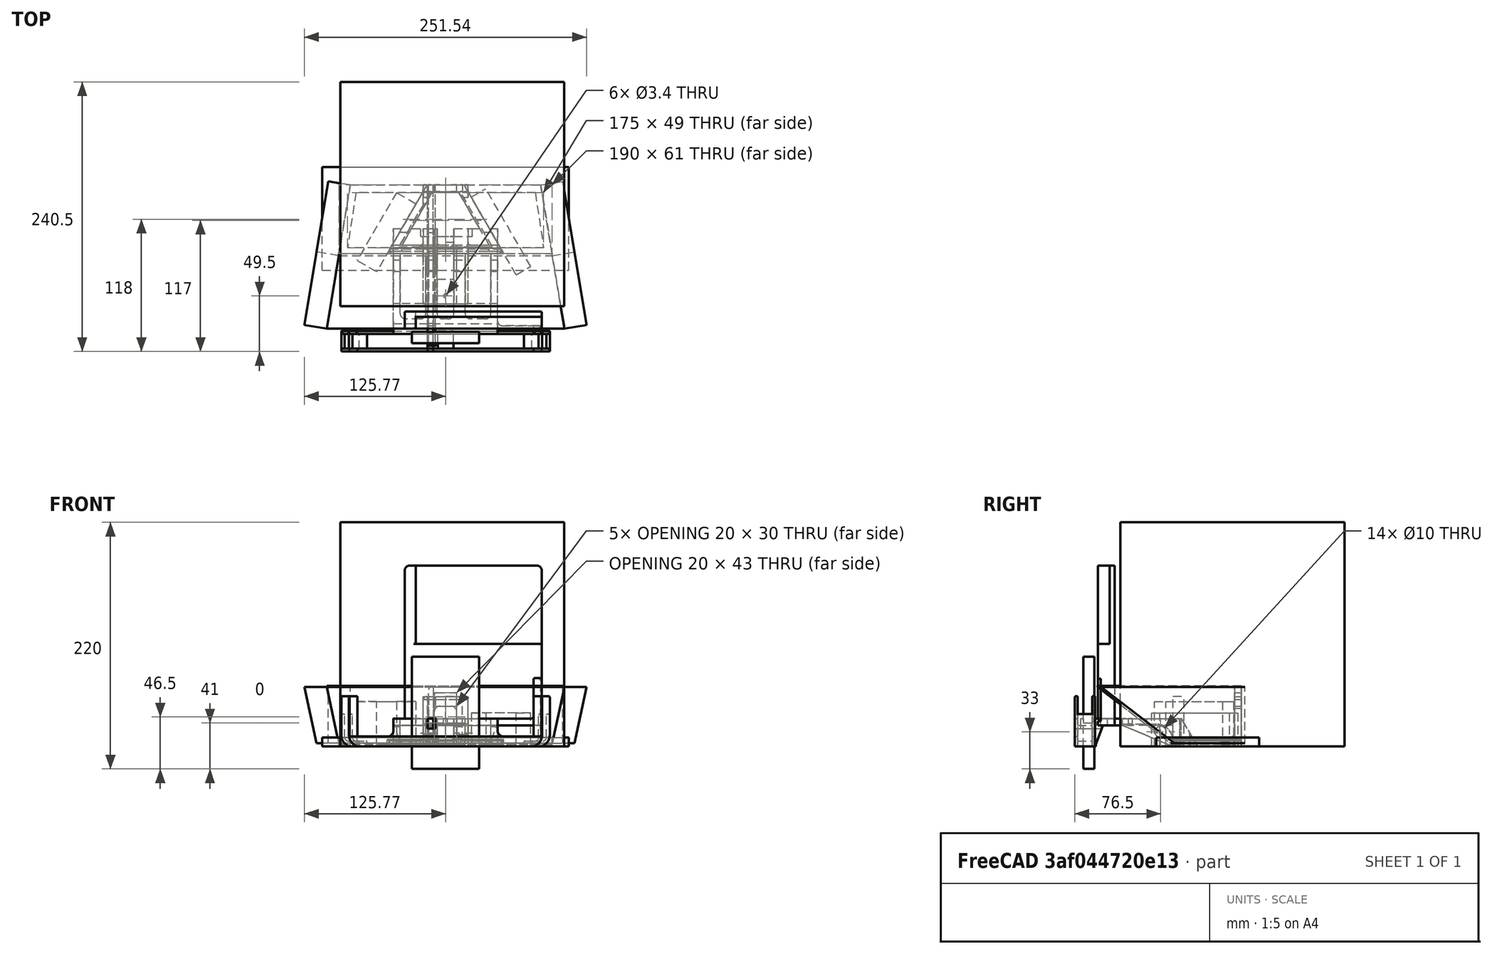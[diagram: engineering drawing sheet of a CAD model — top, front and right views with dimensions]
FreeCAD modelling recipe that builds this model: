
FCSTD DOCUMENT  (FreeCAD 0.20R29603 (Git))
Label: soporte_celular_auto_v3
License: All rights reserved
LicenseURL: http://en.wikipedia.org/wiki/All_rights_reserved
objects: Part::Box×88, Part::Cut×65, Part::Fillet×48, Part::MultiFuse×26, Part::Feature×24, Sketcher::SketchObject×14, Part::Extrusion×12, Part::Cylinder×5, Mesh::Feature×5, Part::Prism×4, PartDesign::Pad×3, PartDesign::Body×3, Part::Chamfer×2, PartDesign::ShapeBinder×2, PartDesign::SubShapeBinder×1
note: 300 computed .brp shape members not serialized (recipe doc carries the construction recipe); baked Part::Feature solids carry a one-line shape summary decoded from their .brp

FEATURE [Sketcher::SketchObject] Sketch001
  FullyConstrained = false
  sketch-geometry (4):
    g0: LineSegment StartX=-95 StartY=0 StartZ=0 EndX=95 EndY=-9e-16 EndZ=0
    g1: LineSegment StartX=-95 StartY=0 StartZ=0 EndX=-85 EndY=61 EndZ=0
    g2: LineSegment StartX=95 StartY=-9e-16 StartZ=0 EndX=85 EndY=61 EndZ=0
    g3: LineSegment StartX=-85 StartY=61 StartZ=0 EndX=85 EndY=61 EndZ=0
  constraints (10):
    c: PointOnObject(g0,g-1)
    c: Symmetric(g0,g0,g-2)
    c: DistanceX(g0,g0) = 190
    c: Coincident(g1,g0)
    c: Coincident(g2,g0)
    c: Coincident(g3,g1)
    c: Coincident(g3,g2)
    c: Symmetric(g1,g2,g-2)
    c: DistanceX(g3,g3) = 170
    c: DistanceY(g0,g2) = 61
FEATURE [Part::Extrusion] Extrude
  Base = -> Sketch001
  Dir = (0,0,1)
  DirMode = 2
  FaceMakerClass = Part::FaceMakerBullseye
  LengthFwd = 10
  LengthRev = 0
  Solid = true
  Symmetric = false
FEATURE [Part::Box] Box  label="Cube"
  AttacherType = Attacher::AttachEngine3D
  Height = 8
  Length = 220
  Placement = pos=(-110,-15,0) rot=(0,0,1;0rad)
  Width = 92
FEATURE [Part::Cut] Cut  label="molde_cortador"
  Base = -> Box
  Tool = -> Extrude
FEATURE [Part::Prism] Prism002
  AttacherType = Attacher::AttachEngine3D
  Circumradius = 60
  FirstAngle = 0
  Height = 6
  Placement = pos=(0,23,0) rot=(0,0,-1;0.523599rad)
  Polygon = 3
  SecondAngle = 0
FEATURE [Part::Prism] Prism003
  AttacherType = Attacher::AttachEngine3D
  Circumradius = 45
  FirstAngle = 0
  Height = 6
  Placement = pos=(0,23,0) rot=(0,0,-1;0.523599rad)
  Polygon = 3
  SecondAngle = 0
FEATURE [Part::Cut] Cut001
  Base = -> Prism002
  Placement = pos=(0,7,0) rot=(0,0,1;0rad)
  Tool = -> Prism003
FEATURE [Part::Box] Box001  label="Cube001"
  AttacherType = Attacher::AttachEngine3D
  Height = 6
  Length = 32
  Placement = pos=(-16,55,0) rot=(0,0,1;0rad)
  Width = 6
FEATURE [Part::MultiFuse] Fusion
  Shapes = -> [Cut001,Box001]
FEATURE [Sketcher::SketchObject] Sketch002
  FullyConstrained = false
  sketch-geometry (4):
    g0: LineSegment StartX=-95 StartY=0 StartZ=0 EndX=95 EndY=-9e-16 EndZ=0
    g1: LineSegment StartX=-95 StartY=0 StartZ=0 EndX=-85 EndY=61 EndZ=0
    g2: LineSegment StartX=95 StartY=-9e-16 StartZ=0 EndX=85 EndY=61 EndZ=0
    g3: LineSegment StartX=-85 StartY=61 StartZ=0 EndX=85 EndY=61 EndZ=0
  constraints (10):
    c: PointOnObject(g0,g-1)
    c: Symmetric(g0,g0,g-2)
    c: DistanceX(g0,g0) = 190
    c: Coincident(g1,g0)
    c: Coincident(g2,g0)
    c: Coincident(g3,g1)
    c: Coincident(g3,g2)
    c: Symmetric(g1,g2,g-2)
    c: DistanceX(g3,g3) = 170
    c: DistanceY(g0,g2) = 61
FEATURE [Part::Box] Box002  label="Cube002"
  AttacherType = Attacher::AttachEngine3D
  Height = 8
  Length = 220
  Placement = pos=(-110,-15,0) rot=(0,0,1;0rad)
  Width = 113
FEATURE [Part::Extrusion] Extrude001
  Base = -> Sketch002
  Dir = (0,0,1)
  DirMode = 2
  FaceMakerClass = Part::FaceMakerBullseye
  LengthFwd = 10
  LengthRev = 0
  Solid = true
  Symmetric = false
FEATURE [Part::Cut] Cut002  label="molde_cortador001"
  Base = -> Box002
  Tool = -> Extrude001
FEATURE [Part::Cut] Cut003  label="base_triangulo"
  Base = -> Fusion
  Tool = -> Cut002
FEATURE [Part::Box] Box003  label="Cube003"
  AttacherType = Attacher::AttachEngine3D
  Height = 3
  Length = 220
  Placement = pos=(-110,2,0) rot=(0,0,1;0rad)
  Width = 2.5
FEATURE [Part::Cut] Cut004  label="base_triangulo_con_canaleta"
  Base = -> Cut003
  Tool = -> Box003
FEATURE [Part::Feature] Fusion001
  shape: bbox 190 x 63 x 3 mm, 10 faces (baked)
FEATURE [Sketcher::SketchObject] Sketch003
  ExternalGeometry = -> [Fusion001]
  FullyConstrained = false
  sketch-geometry (4):
    g0: LineSegment StartX=-87.5 StartY=0 StartZ=0 EndX=87.5 EndY=0 EndZ=0
    g1: LineSegment StartX=-87.5 StartY=0 StartZ=0 EndX=-80 EndY=49 EndZ=0
    g2: LineSegment StartX=87.5 StartY=0 StartZ=0 EndX=80 EndY=49 EndZ=0
    g3: LineSegment StartX=-80 StartY=49 StartZ=0 EndX=80 EndY=49 EndZ=0
  constraints (10):
    c: PointOnObject(g0,g-1)
    c: Symmetric(g0,g0,g-2)
    c: DistanceX(g0,g0) = 175
    c: Coincident(g1,g0)
    c: Coincident(g2,g0)
    c: Coincident(g3,g1)
    c: Coincident(g3,g2)
    c: Symmetric(g1,g2,g-2)
    c: DistanceX(g3,g3) = 160
    c: DistanceY(g0,g2) = 49
FEATURE [Part::Extrusion] Extrude002
  Base = -> Sketch003
  Dir = (0,0,1)
  DirMode = 2
  FaceMakerClass = Part::FaceMakerBullseye
  LengthFwd = 10
  LengthRev = 0
  Placement = pos=(0,5,0) rot=(0,0,1;0rad)
  Solid = true
  Symmetric = false
FEATURE [Part::Cut] Cut004002  label="base"
  Base = -> Fusion001
  Tool = -> Extrude002
FEATURE [Sketcher::SketchObject] Sketch004
  ExternalGeometry = -> [Cut004002]
  FullyConstrained = false
  MapMode = 5
  Placement = pos=(-92.5137,15.1662,-3.7e-15) rot=(-0.51489,0.606172,0.606172;4.09257rad)
  Support = -> [Cut004002]
  sketch-geometry (4):
    g0: LineSegment StartX=-46.4456 StartY=3 StartZ=0 EndX=17.3423 EndY=3 EndZ=0
    g1: LineSegment StartX=-46.4456 StartY=3 StartZ=0 EndX=-46.4456 EndY=53 EndZ=0
    g2: LineSegment StartX=-46.4456 StartY=53 StartZ=0 EndX=83.5544 EndY=53 EndZ=0
    g3: LineSegment StartX=83.5544 StartY=53 StartZ=0 EndX=17.3423 EndY=3 EndZ=0
  constraints (10):
    c: Coincident(g0,g-4)
    c: Coincident(g0,g-3)
    c: Vertical(g1)
    c: Coincident(g0,g1)
    c: DistanceY(g1,g1) = 50
    c: Coincident(g2,g1)
    c: Horizontal(g2)
    c: DistanceX(g2,g2) = 130
    c: Coincident(g3,g2)
    c: Coincident(g3,g0)
FEATURE [Part::Feature] Fusion002
  shape: bbox 190 x 63 x 3 mm, 10 faces (baked)
FEATURE [Sketcher::SketchObject] Sketch005
  ExternalGeometry = -> [Fusion002]
  FullyConstrained = false
  sketch-geometry (4):
    g0: LineSegment StartX=-87.5 StartY=0 StartZ=0 EndX=87.5 EndY=0 EndZ=0
    g1: LineSegment StartX=-87.5 StartY=0 StartZ=0 EndX=-80 EndY=49 EndZ=0
    g2: LineSegment StartX=87.5 StartY=0 StartZ=0 EndX=80 EndY=49 EndZ=0
    g3: LineSegment StartX=-80 StartY=49 StartZ=0 EndX=80 EndY=49 EndZ=0
  constraints (10):
    c: PointOnObject(g0,g-1)
    c: Symmetric(g0,g0,g-2)
    c: DistanceX(g0,g0) = 175
    c: Coincident(g1,g0)
    c: Coincident(g2,g0)
    c: Coincident(g3,g1)
    c: Coincident(g3,g2)
    c: Symmetric(g1,g2,g-2)
    c: DistanceX(g3,g3) = 160
    c: DistanceY(g0,g2) = 49
FEATURE [Part::Extrusion] Extrude003
  Base = -> Sketch005
  Dir = (0,0,1)
  DirMode = 2
  FaceMakerClass = Part::FaceMakerBullseye
  LengthFwd = 10
  LengthRev = 0
  Placement = pos=(0,5,0) rot=(0,0,1;0rad)
  Solid = true
  Symmetric = false
FEATURE [Part::Cut] Cut004003  label="base001"
  Base = -> Fusion002
  Tool = -> Extrude003
FEATURE [Sketcher::SketchObject] Sketch006
  ExternalGeometry = -> [Cut004003]
  FullyConstrained = false
  MapMode = 5
  Placement = pos=(92.5137,15.1662,-2.34e-14) rot=(0.51489,0.606172,0.606172;2.19062rad)
  Support = -> [Cut004003]
  sketch-geometry (4):
    g0: LineSegment StartX=-17.3423 StartY=3 StartZ=0 EndX=46.4456 EndY=3 EndZ=0
    g1: LineSegment StartX=46.4456 StartY=3 StartZ=0 EndX=46.4456 EndY=53 EndZ=0
    g2: LineSegment StartX=46.4456 StartY=53 StartZ=0 EndX=-83.5544 EndY=53 EndZ=0
    g3: LineSegment StartX=-83.5544 StartY=53 StartZ=0 EndX=-17.3423 EndY=3 EndZ=0
  constraints (10):
    c: Coincident(g0,g-4)
    c: Coincident(g0,g-3)
    c: Coincident(g1,g0)
    c: Vertical(g1)
    c: DistanceY(g1,g1) = 50
    c: Coincident(g2,g1)
    c: Horizontal(g2)
    c: Coincident(g3,g2)
    c: DistanceX(g2,g2) = 130
    c: Coincident(g0,g3)
FEATURE [Part::Extrusion] Extrude004
  Base = -> Sketch006
  Dir = (0.986828,0.161775,-2e-16)
  DirMode = 2
  FaceMakerClass = Part::FaceMakerBullseye
  LengthFwd = 20
  LengthRev = 0
  Solid = true
  Symmetric = false
FEATURE [Part::Extrusion] Extrude006
  Base = -> Sketch004
  Dir = (-0.986828,0.161775,-1e-16)
  DirMode = 2
  FaceMakerClass = Part::FaceMakerBullseye
  LengthFwd = 20
  LengthRev = 0
  Solid = true
  Symmetric = false
FEATURE [Sketcher::SketchObject] Sketch
  ExternalGeometry = -> [Extrude006,Extrude004]
  FullyConstrained = false
  sketch-geometry (4):
    g0: LineSegment StartX=-85 StartY=61 StartZ=0 EndX=85 EndY=61 EndZ=0
    g1: LineSegment StartX=-106.031 StartY=-67.2876 StartZ=0 EndX=106.031 EndY=-67.2876 EndZ=0
    g2: LineSegment StartX=-85 StartY=61 StartZ=0 EndX=-106.031 EndY=-67.2876 EndZ=0
    g3: LineSegment StartX=85 StartY=61 StartZ=0 EndX=106.031 EndY=-67.2876 EndZ=0
  constraints (8):
    c: Coincident(g0,g-3)
    c: Coincident(g0,g-4)
    c: Coincident(g1,g-3)
    c: Coincident(g1,g-4)
    c: Coincident(g0,g2)
    c: Coincident(g0,g3)
    c: Coincident(g1,g2)
    c: Coincident(g1,g3)
FEATURE [Part::Extrusion] Extrude007  label="techo_posicion"
  Base = -> Sketch
  Dir = (0,0,1)
  DirMode = 2
  FaceMakerClass = Part::FaceMakerBullseye
  LengthFwd = 1
  LengthRev = 0
  Placement = pos=(0,0,53) rot=(0,0,1;0rad)
  Solid = true
  Symmetric = false
FEATURE [Part::Box] Box004  label="Cube004"
  AttacherType = Attacher::AttachEngine3D
  Height = 44.5
  Length = 40
  Placement = pos=(-20,55,0) rot=(0,0,1;0rad)
  Width = 6
FEATURE [Part::Box] Box005  label="Cube005"
  AttacherType = Attacher::AttachEngine3D
  Height = 30
  Length = 20
  Placement = pos=(-10,55,6) rot=(0,0,1;0rad)
  Width = 6
FEATURE [Part::Cut] Cut004004  label="parte_trasera"
  Base = -> Box004
  Tool = -> Box005
FEATURE [Part::Box] Box006  label="Cube006"
  AttacherType = Attacher::AttachEngine3D
  Height = 6
  Length = 40
  Placement = pos=(0,0,20) rot=(0,0,1;0rad)
  Width = 51
FEATURE [Part::Box] Box007  label="Cube007"
  AttacherType = Attacher::AttachEngine3D
  Height = 6
  Length = 15
  Placement = pos=(12.5,22,20) rot=(0,0,1;0rad)
  Width = 70
FEATURE [Part::Cut] Cut004005
  Base = -> Box006
  Placement = pos=(-20,0,-1) rot=(0,0,1;0rad)
  Tool = -> Box007
FEATURE [Part::Cylinder] Cylinder
  Angle = 360
  AttacherType = Attacher::AttachEngine3D
  FirstAngle = 0
  Height = 30
  Placement = pos=(0,7,0) rot=(0,0,1;0rad)
  Radius = 1.7
  SecondAngle = 0
FEATURE [Part::Cut] Cut004006
  Base = -> Cut004005
  Placement = pos=(0,-45,0) rot=(0,0,1;0rad)
  Tool = -> Cylinder
FEATURE [Part::Box] Box008  label="celular"
  AttacherType = Attacher::AttachEngine3D
  Height = 100
  Length = 60
  Placement = pos=(-30,-80,-20) rot=(0,0,1;0rad)
  Width = 10
FEATURE [Part::Box] Box009  label="Cube008"
  AttacherType = Attacher::AttachEngine3D
  Height = 22
  Length = 12.5
  Placement = pos=(7.5,0,3) rot=(0,0,1;0rad)
  Width = 7.5
FEATURE [Part::Box] Box010  label="Cube009"
  AttacherType = Attacher::AttachEngine3D
  Height = 22
  Length = 12.5
  Placement = pos=(-20,0,3) rot=(0,0,1;0rad)
  Width = 7.5
FEATURE [Part::Feature] Fusion004001  label="Fusion005"
  shape: bbox 99.53 x 106 x 53 mm, 44 faces (baked)
FEATURE [Part::Fillet] Fillet006
  Base = -> Fusion004001
  Edges = 2 edges r=15: [Edge75,Edge79]
FEATURE [Part::Fillet] Fillet007
  Base = -> Fillet006
  Edges = 2 edges r=2: [Edge65,Edge67]
FEATURE [Part::Fillet] Fillet008  label="soporte_final_v2.1_00"
  Base = -> Fillet007
  Edges = 2 edges r=2: [Edge3,Edge19]
FEATURE [Part::Feature] Fillet008001  label="soporte_final_v2.002"
  shape: bbox 99.53 x 106 x 53 mm, 50 faces (baked)
FEATURE [Part::Box] Box011  label="Cube010"
  AttacherType = Attacher::AttachEngine3D
  Height = 100
  Length = 70
  Placement = pos=(10,-51,0) rot=(0,0,1;0rad)
  Width = 120
FEATURE [Part::Cut] Cut004007
  Base = -> Fillet008001
  Tool = -> Box011
FEATURE [Part::Box] Box012  label="Cube011"
  AttacherType = Attacher::AttachEngine3D
  Height = 100
  Length = 70
  Placement = pos=(-11,13,0) rot=(0,0,1;0rad)
  Width = 120
FEATURE [Part::Cut] Cut004008
  Base = -> Cut004007
  Tool = -> Box012
FEATURE [Part::Box] Box013  label="Cube012"
  AttacherType = Attacher::AttachEngine3D
  Height = 10
  Length = 40
  Placement = pos=(-60,0,2) rot=(0,0,1;0rad)
  Width = 70
FEATURE [Part::Cut] Cut004009
  Base = -> Cut004008
  Tool = -> Box013
FEATURE [Part::Box] Box014  label="Cube013"
  AttacherType = Attacher::AttachEngine3D
  Height = 50
  Length = 19
  Placement = pos=(-30,-60,0) rot=(0,0,1;0rad)
  Width = 60
FEATURE [Part::Cut] Cut004010
  Base = -> Cut004009
  Tool = -> Box014
FEATURE [Part::Box] Box015  label="Cube014"
  AttacherType = Attacher::AttachEngine3D
  Height = 30
  Length = 10
  Placement = pos=(-21,0,2) rot=(0,0,1;0rad)
  Width = 10
FEATURE [Part::Cut] Cut004011
  Base = -> Cut004010
  Tool = -> Box015
FEATURE [Part::Fillet] Fillet008002  label="soporte_final_v2.1"
  Base = -> Fillet008
  Edges = 4 edges r=3: [Edge7,Edge53,Edge58,Edge60]
FEATURE [Part::Box] Box016  label="Cube015"
  AttacherType = Attacher::AttachEngine3D
  Height = 10
  Length = 40
  Placement = pos=(-54,-7,0) rot=(0,0,1;0rad)
  Width = 10
FEATURE [Part::Cut] Cut004012  label="test"
  Base = -> Cut004011
  Tool = -> Box016
FEATURE [Part::MultiFuse] Fusion004002
  Shapes = -> [Cut004006,Box009,Box010]
FEATURE [Part::Box] Box017  label="Cube016"
  AttacherType = Attacher::AttachEngine3D
  Height = 22
  Length = 12.5
  Placement = pos=(7.5,0,3) rot=(0,0,1;0rad)
  Width = 7.5
FEATURE [Part::Cylinder] Cylinder001
  Angle = 360
  AttacherType = Attacher::AttachEngine3D
  FirstAngle = 0
  Height = 30
  Placement = pos=(0,7,0) rot=(0,0,1;0rad)
  Radius = 1.7
  SecondAngle = 0
FEATURE [Part::Box] Box018  label="Cube017"
  AttacherType = Attacher::AttachEngine3D
  Height = 6
  Length = 40
  Placement = pos=(0,0,20) rot=(0,0,1;0rad)
  Width = 51
FEATURE [Part::Box] Box019  label="Cube018"
  AttacherType = Attacher::AttachEngine3D
  Height = 6
  Length = 15
  Placement = pos=(12.5,22,20) rot=(0,0,1;0rad)
  Width = 70
FEATURE [Part::Cut] Cut004013
  Base = -> Box018
  Placement = pos=(-20,0,-1) rot=(0,0,1;0rad)
  Tool = -> Box019
FEATURE [Part::Cut] Cut004014
  Base = -> Cut004013
  Placement = pos=(0,-45,0) rot=(0,0,1;0rad)
  Tool = -> Cylinder001
FEATURE [Part::Box] Box020  label="Cube019"
  AttacherType = Attacher::AttachEngine3D
  Height = 22
  Length = 12.5
  Placement = pos=(-20,0,3) rot=(0,0,1;0rad)
  Width = 7.5
FEATURE [Part::MultiFuse] Fusion004004
  Shapes = -> [Cut004014,Box017,Box020]
FEATURE [Sketcher::SketchObject] Sketch007
  ExternalGeometry = -> [Fusion004002,Cut004]
  FullyConstrained = true
  MapMode = 5
  Placement = pos=(-20,0,0) rot=(0.57735,-0.57735,-0.57735;2.0944rad)
  Support = -> [Fusion004002]
  sketch-geometry (3):
    g0: LineSegment StartX=0 StartY=0 StartZ=0 EndX=0 EndY=19 EndZ=0
    g1: LineSegment StartX=0 StartY=19 StartZ=0 EndX=45 EndY=19 EndZ=0
    g2: LineSegment StartX=45 StartY=19 StartZ=0 EndX=0 EndY=0 EndZ=0
  constraints (7):
    c: PointOnObject(g0,g-1)
    c: Vertical(g0)
    c: Coincident(g1,g0)
    c: Coincident(g0,g-3)
    c: Coincident(g1,g-3)
    c: Coincident(g2,g1)
    c: Coincident(g2,g0)
FEATURE [Part::Extrusion] Extrude008
  Base = -> Sketch007
  Dir = (-1,0,0)
  DirMode = 2
  FaceMakerClass = Part::FaceMakerBullseye
  LengthFwd = 0
  LengthRev = 39
  Placement = pos=(-26.5,0,0) rot=(0,0,1;0rad)
  Solid = true
  Symmetric = false
FEATURE [Part::Extrusion] Extrude009
  Base = -> Sketch007
  Dir = (-1,0,0)
  DirMode = 2
  FaceMakerClass = Part::FaceMakerBullseye
  LengthFwd = 39
  LengthRev = 0
  Placement = pos=(66.5,0,0) rot=(0,0,1;0rad)
  Solid = true
  Symmetric = false
FEATURE [Sketcher::SketchObject] Sketch008
  ExternalGeometry = -> [Fusion004002,Cut004]
  FullyConstrained = true
  MapMode = 5
  Placement = pos=(-20,0,0) rot=(0.57735,-0.57735,-0.57735;2.0944rad)
  Support = -> [Fusion004002]
  sketch-geometry (3):
    g0: LineSegment StartX=-7.5 StartY=0 StartZ=0 EndX=-7.5 EndY=25 EndZ=0
    g1: LineSegment StartX=-7.5 StartY=25 StartZ=0 EndX=-21.9338 EndY=0 EndZ=0
    g2: LineSegment StartX=-21.9338 StartY=0 StartZ=0 EndX=-7.5 EndY=0 EndZ=0
  constraints (8):
    c: Vertical(g0)
    c: Coincident(g0,g1)
    c: Coincident(g1,g2)
    c: Horizontal(g2)
    c: Coincident(g0,g2)
    c: Angle(g2,g1) = 1.0472
    c: DistanceY(g0,g-1) = 0
    c: Coincident(g0,g-3)
FEATURE [Part::Extrusion] Extrude010
  Base = -> Sketch008
  Dir = (-1,0,0)
  DirMode = 2
  FaceMakerClass = Part::FaceMakerBullseye
  LengthFwd = -39
  LengthRev = 0
  Placement = pos=(-26.5,0,0) rot=(0,0,1;0rad)
  Solid = true
  Symmetric = false
FEATURE [Part::Box] Box021  label="Cube020"
  AttacherType = Attacher::AttachEngine3D
  Height = 22
  Length = 12.5
  Placement = pos=(7.5,0,3) rot=(0,0,1;0rad)
  Width = 7.5
FEATURE [Sketcher::SketchObject] Sketch009
  FullyConstrained = false
  sketch-geometry (4):
    g0: LineSegment StartX=-95 StartY=0 StartZ=0 EndX=95 EndY=-9e-16 EndZ=0
    g1: LineSegment StartX=-95 StartY=0 StartZ=0 EndX=-85 EndY=61 EndZ=0
    g2: LineSegment StartX=95 StartY=-9e-16 StartZ=0 EndX=85 EndY=61 EndZ=0
    g3: LineSegment StartX=-85 StartY=61 StartZ=0 EndX=85 EndY=61 EndZ=0
  constraints (10):
    c: PointOnObject(g0,g-1)
    c: Symmetric(g0,g0,g-2)
    c: DistanceX(g0,g0) = 190
    c: Coincident(g1,g0)
    c: Coincident(g2,g0)
    c: Coincident(g3,g1)
    c: Coincident(g3,g2)
    c: Symmetric(g1,g2,g-2)
    c: DistanceX(g3,g3) = 170
    c: DistanceY(g0,g2) = 61
FEATURE [Part::Extrusion] Extrude011
  Base = -> Sketch009
  Dir = (0,0,1)
  DirMode = 2
  FaceMakerClass = Part::FaceMakerBullseye
  LengthFwd = 10
  LengthRev = 0
  Solid = true
  Symmetric = false
FEATURE [Part::Cylinder] Cylinder002
  Angle = 360
  AttacherType = Attacher::AttachEngine3D
  FirstAngle = 0
  Height = 30
  Placement = pos=(0,7,0) rot=(0,0,1;0rad)
  Radius = 1.7
  SecondAngle = 0
FEATURE [Part::Prism] Prism004
  AttacherType = Attacher::AttachEngine3D
  Circumradius = 45
  FirstAngle = 0
  Height = 6
  Placement = pos=(0,23,0) rot=(0,0,-1;0.523599rad)
  Polygon = 3
  SecondAngle = 0
FEATURE [Part::Box] Box022  label="Cube021"
  AttacherType = Attacher::AttachEngine3D
  Height = 6
  Length = 40
  Placement = pos=(0,0,20) rot=(0,0,1;0rad)
  Width = 51
FEATURE [Part::Box] Box023  label="Cube022"
  AttacherType = Attacher::AttachEngine3D
  Height = 3
  Length = 220
  Placement = pos=(-110,2,0) rot=(0,0,1;0rad)
  Width = 2.5
FEATURE [Part::Box] Box024  label="Cube023"
  AttacherType = Attacher::AttachEngine3D
  Height = 8
  Length = 220
  Placement = pos=(-110,-15,0) rot=(0,0,1;0rad)
  Width = 113
FEATURE [Part::Cut] Cut004020  label="molde_cortador002"
  Base = -> Box024
  Tool = -> Extrude011
FEATURE [Part::Prism] Prism005
  AttacherType = Attacher::AttachEngine3D
  Circumradius = 60
  FirstAngle = 0
  Height = 6
  Placement = pos=(0,23,0) rot=(0,0,-1;0.523599rad)
  Polygon = 3
  SecondAngle = 0
FEATURE [Part::Cut] Cut004019
  Base = -> Prism005
  Placement = pos=(0,7,0) rot=(0,0,1;0rad)
  Tool = -> Prism004
FEATURE [Part::Box] Box025  label="Cube024"
  AttacherType = Attacher::AttachEngine3D
  Height = 6
  Length = 15
  Placement = pos=(12.5,22,20) rot=(0,0,1;0rad)
  Width = 70
FEATURE [Part::Cut] Cut004017
  Base = -> Box022
  Placement = pos=(-20,0,-1) rot=(0,0,1;0rad)
  Tool = -> Box025
FEATURE [Part::Cut] Cut004018
  Base = -> Cut004017
  Placement = pos=(0,-45,0) rot=(0,0,1;0rad)
  Tool = -> Cylinder002
FEATURE [Part::Box] Box026  label="Cube025"
  AttacherType = Attacher::AttachEngine3D
  Height = 6
  Length = 32
  Placement = pos=(-16,55,0) rot=(0,0,1;0rad)
  Width = 6
FEATURE [Part::MultiFuse] Fusion004005
  Shapes = -> [Cut004019,Box026]
FEATURE [Part::Cut] Cut004015  label="base_triangulo001"
  Base = -> Fusion004005
  Tool = -> Cut004020
FEATURE [Part::Cut] Cut004016  label="base_triangulo_con_canaleta001"
  Base = -> Cut004015
  Tool = -> Box023
FEATURE [Part::Box] Box027  label="Cube026"
  AttacherType = Attacher::AttachEngine3D
  Height = 22
  Length = 12.5
  Placement = pos=(-20,0,3) rot=(0,0,1;0rad)
  Width = 7.5
FEATURE [Part::MultiFuse] Fusion004006
  Shapes = -> [Cut004018,Box021,Box027]
FEATURE [Sketcher::SketchObject] Sketch010
  ExternalGeometry = -> [Fusion004006,Cut004016]
  FullyConstrained = false
  MapMode = 5
  Placement = pos=(-20,0,0) rot=(0.57735,-0.57735,-0.57735;2.0944rad)
  Support = -> [Fusion004006]
  sketch-geometry (3):
    g0: LineSegment StartX=-7.5 StartY=0 StartZ=0 EndX=-7.5 EndY=25 EndZ=0
    g1: LineSegment StartX=-7.5 StartY=25 StartZ=0 EndX=-21.9338 EndY=0 EndZ=0
    g2: LineSegment StartX=-21.9338 StartY=0 StartZ=0 EndX=-7.5 EndY=0 EndZ=0
  constraints (8):
    c: Vertical(g0)
    c: Coincident(g0,g1)
    c: Coincident(g1,g2)
    c: Horizontal(g2)
    c: Coincident(g0,g2)
    c: Angle(g2,g1) = 1.0472
    c: DistanceY(g0,g-1) = 0
    c: Coincident(g0,g-3)
FEATURE [Part::Extrusion] Extrude012
  Base = -> Sketch010
  Dir = (-1,0,0)
  DirMode = 2
  FaceMakerClass = Part::FaceMakerBullseye
  LengthFwd = -39
  LengthRev = 0
  Placement = pos=(27.5,0,0) rot=(0,0,1;0rad)
  Solid = true
  Symmetric = false
FEATURE [Part::MultiFuse] Fusion004007
  Shapes = -> [Extrude010,Extrude012,Extrude009,Extrude008,Fusion004002]
FEATURE [Part::MultiFuse] Fusion004008  label="parte_frontal"
  Shapes = -> [Fusion004006,Fusion004007]
FEATURE [Part::MultiFuse] Fusion004009  label="pieza_sin_refinar"
  Shapes = -> [Cut004004,Cut004016,Fusion004008]
FEATURE [Part::Feature] Fusion004009001  label="pieza_sin_refinar001"
  shape: bbox 103.9 x 106 x 42 mm, 40 faces (baked)
FEATURE [Part::Fillet] Fillet
  Base = -> Fusion004009001
  Edges = 12 edges r=2: [Edge4,Edge8,Edge38,Edge44,Edge56,Edge57,Edge60,Edge62,Edge64,Edge66,Edge67,Edge68]
FEATURE [Part::Fillet] Fillet008003
  Base = -> Fillet
  Edges = 2 edges r=2: [Edge92,Edge98]
FEATURE [Part::Fillet] Fillet008004
  Base = -> Fillet008003
  Edges = 4 edges r=2: [Edge22,Edge28,Edge83,Edge88]
FEATURE [Part::Fillet] Fillet008005
  Base = -> Fillet008004
  Edges = 4 edges r=5: [Edge105,Edge107,Edge108,Edge111]
FEATURE [Part::Fillet] Fillet008006
  Base = -> Fillet008005
  Edges = 2 edges r=1: [Edge107,Edge131]
FEATURE [Part::Fillet] Fillet008007
  Base = -> Fillet008006
  Edges = 2 edges r=2: [Edge3,Edge23]
FEATURE [Part::Chamfer] Chamfer  label="soporte_v2.2"
  Base = -> Fillet008007
  Edges = 2 edges r=5: [Edge154,Edge156]
FEATURE [Part::Box] Box028  label="Cube027"
  AttacherType = Attacher::AttachEngine3D
  Height = 113
  Length = 109
  Placement = pos=(-10,-55,0) rot=(0,0,1;0rad)
  Width = 156
FEATURE [Part::Feature] Chamfer001  label="soporte_v2.2_for_test"
  shape: bbox 101 x 106 x 42 mm, 68 faces (baked)
FEATURE [Part::Cut] Cut004021  label="test_v2.2"
  Base = -> Chamfer001
  Tool = -> Box028
FEATURE [Part::Box] Box029  label="Cube028"
  AttacherType = Attacher::AttachEngine3D
  Height = 6
  Length = 78
  Placement = pos=(-39,0,0) rot=(0,0,1;0rad)
  Width = 15
FEATURE [Part::MultiFuse] Fusion004009002  label="pieza_sin_refinar_reforzada"
  Shapes = -> [Fusion004009,Box029]
FEATURE [Part::Box] Box030  label="Cube029"
  AttacherType = Attacher::AttachEngine3D
  Height = 45
  Length = 10
  Width = 10
FEATURE [Part::Box] Box031  label="Cube030"
  AttacherType = Attacher::AttachEngine3D
  Height = 16
  Length = 46
  Placement = pos=(-22,15,0) rot=(0,0,1;0rad)
  Width = 15
FEATURE [Part::Cut] Cut004022  label="pieza_sin_refinar_v2.3"
  Base = -> Fusion004009002
  Tool = -> Box031
FEATURE [Part::Feature] Cut004022001  label="pieza_sin_refinar_v2.004"
  shape: bbox 103.9 x 106 x 44.5 mm, 42 faces (baked)
FEATURE [Part::Fillet] Fillet008008
  Base = -> Cut004022001
  Edges = 2 edges r=5: [Edge111,Edge116]
FEATURE [Part::Fillet] Fillet008009
  Base = -> Fillet008008
  Edges = 4 edges r=5: [Edge69,Edge70,Edge71,Edge72]
FEATURE [Part::Fillet] Fillet008010
  Base = -> Fillet008009
  Edges = 2 edges r=5: [Edge41,Edge54]
FEATURE [Part::Fillet] Fillet008011
  Base = -> Fillet008010
  Edges = 4 edges r=3: [Edge73,Edge86,Edge90,Edge106]
FEATURE [Part::Fillet] Fillet008012
  Base = -> Fillet008011
  Edges = 2 edges r=3: [Edge130,Edge134]
FEATURE [Part::Fillet] Fillet008013
  Base = -> Fillet008012
  Edges = 4 edges r=3: [Edge54,Edge59,Edge71,Edge75]
FEATURE [Part::Fillet] Fillet008014  label="pieza_v2.3"
  Base = -> Fillet008013
  Edges = 4 edges r=3: [Edge10,Edge55,Edge72,Edge79]
FEATURE [Part::Box] Box032  label="Cube031"
  AttacherType = Attacher::AttachEngine3D
  Height = 22
  Length = 39
  Placement = pos=(7.5,0,3) rot=(0,0,1;0rad)
  Width = 7.5
FEATURE [Part::Box] Box033  label="Cube032"
  AttacherType = Attacher::AttachEngine3D
  Height = 22
  Length = 39
  Placement = pos=(-46.5,0,3) rot=(0,0,1;0rad)
  Width = 7.5
FEATURE [Part::MultiFuse] Fusion004009003
  Shapes = -> [Fusion004008,Box032,Box033]
FEATURE [Part::Box] Box034  label="Cube033"
  AttacherType = Attacher::AttachEngine3D
  Height = 6
  Length = 30
  Placement = pos=(-46.5,-45,19) rot=(0,0,1;0rad)
  Width = 50
FEATURE [Part::Box] Box035  label="Cube034"
  AttacherType = Attacher::AttachEngine3D
  Height = 6
  Length = 31
  Placement = pos=(15.5,-45,19) rot=(0,0,1;0rad)
  Width = 50
FEATURE [Part::MultiFuse] Fusion004009004
  Shapes = -> [Fillet008014,Fusion004009003,Box034,Box035]
FEATURE [Part::Box] Box036  label="Cube035"
  AttacherType = Attacher::AttachEngine3D
  Height = 3
  Length = 100
  Placement = pos=(-50,2,0) rot=(0,0,1;0rad)
  Width = 2.5
FEATURE [Part::Cut] Cut004022002
  Base = -> Fusion004009004
  Tool = -> Box036
FEATURE [PartDesign::ShapeBinder] CopyCut004022002
  TraceSupport = false
FEATURE [Sketcher::SketchObject] Sketch011
  FullyConstrained = true
  MapMode = 5
  Placement = pos=(38.9711,22.5,0) rot=(0.377964,0.654654,0.654654;2.41886rad)
  Support = -> [CopyCut004022002]
  sketch-geometry (4):
    g0: LineSegment StartX=-48 StartY=0 StartZ=0 EndX=-48 EndY=30 EndZ=0
    g1: LineSegment StartX=-48 StartY=30 StartZ=0 EndX=32 EndY=30 EndZ=0
    g2: LineSegment StartX=32 StartY=30 StartZ=0 EndX=32 EndY=0 EndZ=0
    g3: LineSegment StartX=32 StartY=0 StartZ=0 EndX=-48 EndY=0 EndZ=0
  constraints (12):
    c: PointOnObject(g0,g-1)
    c: Vertical(g0)
    c: Coincident(g0,g1)
    c: Horizontal(g1)
    c: Coincident(g1,g2)
    c: Vertical(g2)
    c: Coincident(g2,g3)
    c: Horizontal(g3)
    c: Coincident(g3,g0)
    c: DistanceX(g1,g1) = 80
    c: DistanceY(g0,g0) = 30
    c: DistanceX(g-1,g1) = 32
FEATURE [PartDesign::Pad] Pad
  Direction = (1,1,1)
  Length = 15
  Length2 = 100
  Profile = -> Sketch011
  Type = 0
FEATURE [PartDesign::Body] Body
  Group = -> [CopyCut004022002,Sketch011,Pad]
  Origin = -> Origin
  Tip = -> Pad
FEATURE [PartDesign::ShapeBinder] CopyCut004022002001
  TraceSupport = false
FEATURE [Sketcher::SketchObject] Sketch012
  FullyConstrained = true
  MapMode = 5
  Placement = pos=(-38.9711,22.5,0) rot=(-0.377964,0.654654,0.654654;3.86433rad)
  Support = -> [CopyCut004022002001]
  sketch-geometry (4):
    g0: LineSegment StartX=-25 StartY=0 StartZ=0 EndX=45 EndY=0 EndZ=0
    g1: LineSegment StartX=45 StartY=0 StartZ=0 EndX=45 EndY=40 EndZ=0
    g2: LineSegment StartX=45 StartY=40 StartZ=0 EndX=-25 EndY=40 EndZ=0
    g3: LineSegment StartX=-25 StartY=40 StartZ=0 EndX=-25 EndY=0 EndZ=0
  constraints (12):
    c: Coincident(g0,g1)
    c: Coincident(g1,g2)
    c: Coincident(g2,g3)
    c: Coincident(g3,g0)
    c: Horizontal(g0)
    c: Horizontal(g2)
    c: Vertical(g1)
    c: Vertical(g3)
    c: PointOnObject(g0,g-1)
    c: DistanceX(g2,g2) = 70
    c: DistanceY(g1,g1) = 40
    c: DistanceX(g0,g-1) = 25
FEATURE [PartDesign::Pad] Pad001
  Direction = (1,1,1)
  Length = 20
  Length2 = 100
  Profile = -> Sketch012
  Type = 0
FEATURE [PartDesign::Body] Body001
  Group = -> [CopyCut004022002001,Sketch012,Pad001]
  Origin = -> Origin001
  Tip = -> Pad001
FEATURE [Part::Feature] Cut004022002_solid  label="Cut004022002 (Solid)"
  shape: bbox 99.53 x 106 x 44.5 mm, 121 faces (baked)
FEATURE [Part::Feature] Body002
  shape: bbox 52.99 x 76.78 x 30 mm, 6 faces (baked)
FEATURE [Part::Feature] Body001001
  shape: bbox 52.32 x 70.62 x 40 mm, 6 faces (baked)
FEATURE [Part::Cut] Cut004022003
  Base = -> Cut004022002_solid
  Tool = -> Body002
FEATURE [Part::Cut] Cut004022004
  Base = -> Cut004022003
  Tool = -> Body001001
FEATURE [Part::Box] Box037  label="Cube036"
  AttacherType = Attacher::AttachEngine3D
  Height = 6
  Length = 93
  Placement = pos=(-46.5,-64.5,19) rot=(0,0,1;0rad)
  Width = 32
FEATURE [Part::MultiFuse] Fusion004009005
  Shapes = -> [Cut004022004,Box037]
FEATURE [Part::Box] Box038  label="Cube037"
  AttacherType = Attacher::AttachEngine3D
  Height = 30
  Length = 15
  Placement = pos=(-7.5,-58.5,0) rot=(0,0,1;0rad)
  Width = 50
FEATURE [Part::Box] Box039  label="Cube038"
  AttacherType = Attacher::AttachEngine3D
  Height = 30
  Length = 23
  Placement = pos=(17.5,-58.5,0) rot=(0,0,1;0rad)
  Width = 58.5
FEATURE [Part::Box] Box040  label="Cube039"
  AttacherType = Attacher::AttachEngine3D
  Height = 30
  Length = 23
  Placement = pos=(-40.5,-58.5,0) rot=(0,0,1;0rad)
  Width = 58.5
FEATURE [Part::Cut] Cut004022005
  Base = -> Fusion004009005
  Tool = -> Box038
FEATURE [Part::Cut] Cut004022006
  Base = -> Cut004022005
  Tool = -> Box040
FEATURE [Part::Cut] Cut004022007
  Base = -> Cut004022006
  Tool = -> Box039
FEATURE [Part::Fillet] Fillet008015
  Base = -> Cut004022007
  Edges = 4 edges r=5: [Edge49,Edge53,Edge65,Edge70]
FEATURE [Part::Fillet] Fillet008016
  Base = -> Fillet008015
  Edges = 4 edges r=1: [Edge28,Edge47,Edge61,Edge77]
FEATURE [Part::Fillet] Fillet008017
  Base = -> Fillet008016
  Edges = 1 edges r=1: [Edge269]
FEATURE [Part::Fillet] Fillet008018
  Base = -> Fillet008017
  Edges = 1 edges r=1: [Edge347]
FEATURE [Part::Fillet] Fillet008019
  Base = -> Fillet008018
  Edges = 2 edges r=5: [Edge236,Edge297]
FEATURE [Part::Fillet] Fillet008020
  Base = -> Fillet008019
  Edges = 2 edges r=3: [Edge392,Edge439]
FEATURE [Part::Cylinder] Cylinder003
  Angle = 360
  AttacherType = Attacher::AttachEngine3D
  FirstAngle = 0
  Height = 100
  Placement = pos=(-50,-11,13) rot=(0,1,0;1.5708rad)
  Radius = 5
  SecondAngle = 0
FEATURE [Part::Cut] Cut004022008  label="frontal_solo_soporte"
  Base = -> Fillet008020
  Tool = -> Cylinder003
FEATURE [Part::Box] Box041  label="base_sofporte_celular"
  AttacherType = Attacher::AttachEngine3D
  Height = 40
  Length = 166.2
  Width = 13
FEATURE [Part::Box] Box042  label="base_sofporte_celular001"
  AttacherType = Attacher::AttachEngine3D
  Height = 45
  Length = 172.2
  Placement = pos=(-3,-2.5,-5) rot=(0,0,1;0rad)
  Width = 18
FEATURE [Part::Cut] Cut004022009
  Base = -> Box042
  Placement = pos=(-83.1,-80,20) rot=(0,0,1;0rad)
  Tool = -> Box041
FEATURE [Part::Box] Box043  label="base_sofporte_celular002"
  AttacherType = Attacher::AttachEngine3D
  Height = 40
  Length = 157.2
  Placement = pos=(-78.6,-87.5,24) rot=(0,0,1;0rad)
  Width = 25
FEATURE [Part::Cut] Cut004022010
  Base = -> Cut004022009
  Tool = -> Box043
FEATURE [Part::Box] Box044  label="Cube040"
  AttacherType = Attacher::AttachEngine3D
  Height = 100
  Length = 100
  Placement = pos=(-9,-91,0) rot=(0,0,1;0rad)
  Width = 200
FEATURE [Part::Box] Box045  label="Cube041"
  AttacherType = Attacher::AttachEngine3D
  Height = 100
  Length = 100
  Placement = pos=(-115,-91,0) rot=(0,0,1;0rad)
  Width = 200
FEATURE [Part::Box] Box046  label="Cube042"
  AttacherType = Attacher::AttachEngine3D
  Height = 3
  Length = 6
  Placement = pos=(-15,0,0) rot=(0,0,1;0rad)
  Width = 57
FEATURE [Part::Box] Box047  label="Cube043"
  AttacherType = Attacher::AttachEngine3D
  Height = 29
  Length = 10
  Placement = pos=(-17,0,3) rot=(0,0,1;0rad)
  Width = 55
FEATURE [Part::Box] Box048  label="Cube044"
  AttacherType = Attacher::AttachEngine3D
  Height = 200
  Length = 200
  Placement = pos=(-100,-66,0) rot=(0,0,1;0rad)
  Width = 200
FEATURE [Part::Box] Box049  label="Cube045"
  AttacherType = Attacher::AttachEngine3D
  Height = 200
  Length = 200
  Placement = pos=(-100,-281,0) rot=(0,0,1;0rad)
  Width = 200
FEATURE [Part::Box] Box052  label="Cube048"
  AttacherType = Attacher::AttachEngine3D
  Height = 20
  Length = 140
  Placement = pos=(-70,-80,9) rot=(0,0,1;0rad)
  Width = 13
FEATURE [Part::Cut] Cut004022017  label="frontal_solo_celular1"
  Base = -> Cut004022010
  Placement = pos=(0,-5,-25) rot=(0,0,1;0rad)
  Tool = -> Box052
FEATURE [Part::Feature] Fillet008027011001  label="soporte_v3_003"
  shape: bbox 173.4 x 143.5 x 61 mm, 224 faces (baked)
FEATURE [Part::Cut] Cut004022018
  Base = -> Fillet008027011001
  Tool = -> Box045
FEATURE [Part::Cut] Cut004022019
  Base = -> Cut004022018
  Tool = -> Box044
FEATURE [Part::Box] Box053  label="Cube049"
  AttacherType = Attacher::AttachEngine3D
  Height = 5
  Length = 6
  Placement = pos=(-15,-82,16) rot=(0,0,1;0rad)
  Width = 17
FEATURE [Part::MultiFuse] Fusion004009009
  Shapes = -> [Cut004022019,Box046]
FEATURE [Part::MultiFuse] Fusion004009010
  Shapes = -> [Fusion004009009,Box053]
FEATURE [Part::Cut] Cut004022020
  Base = -> Fusion004009010
  Tool = -> Box047
FEATURE [Part::Chamfer] Chamfer002  label="test_v3_1"
  Base = -> Cut004022020
  Edges = 1 edges r=2: [Edge78]
FEATURE [Part::Feature] Fillet008027011008001  label="soporte_v3_004"
  shape: bbox 173.7 x 143.7 x 61.22 mm, 236 faces, 0 solids (baked)
FEATURE [Part::Cut] Cut004022021
  Base = -> Fillet008027011008001
  Tool = -> Box048
FEATURE [Part::Cut] Cut004022022  label="test_v3_2"
  Base = -> Cut004022021
  Tool = -> Box049
FEATURE [Mesh::Feature] Mesh002  label="test_v3_2 (Meshed)"
FEATURE [Part::Feature] Fillet008027011008_solid  label="soporte_v3_2 (Solid)"
  shape: bbox 173.7 x 143.7 x 61.22 mm, 236 faces (baked)
FEATURE [Part::Box] Box054  label="Cube050"
  AttacherType = Attacher::AttachEngine3D
  Height = 200
  Length = 200
  Placement = pos=(-94,-47,0) rot=(0,0,1;0rad)
  Width = 200
FEATURE [Part::Feature] Fillet008027011008_solid001  label="soporte_v3_2 (Solid)001"
  shape: bbox 173.7 x 143.7 x 61.22 mm, 236 faces (baked)
FEATURE [Part::Box] Box055  label="Cube051"
  AttacherType = Attacher::AttachEngine3D
  Height = 200
  Length = 200
  Placement = pos=(-94,-247,0) rot=(0,0,1;0rad)
  Width = 200
FEATURE [Part::Cut] Cut004022023
  Base = -> Fillet008027011008_solid
  Refine = true
  Tool = -> Box055
FEATURE [Part::Box] Box056  label="Cube052"
  AttacherType = Attacher::AttachEngine3D
  Height = 6
  Length = 93
  Placement = pos=(-46.5,-72,19) rot=(0,0,1;0rad)
  Width = 8
FEATURE [Part::Box] Box057  label="Cube053"
  AttacherType = Attacher::AttachEngine3D
  Height = 200
  Length = 200
  Placement = pos=(-216,-97,0) rot=(0,0,1;0rad)
  Width = 200
FEATURE [Part::Box] Box058  label="Cube054"
  AttacherType = Attacher::AttachEngine3D
  Height = 200
  Length = 200
  Placement = pos=(-11,-97,0) rot=(0,0,1;0rad)
  Width = 200
FEATURE [Part::Box] Box059  label="Cube055"
  AttacherType = Attacher::AttachEngine3D
  Height = 20
  Length = 10
  Placement = pos=(-18,40,6) rot=(0,0,1;0rad)
  Width = 15
FEATURE [Part::Feature] Body001002
  shape: bbox 52.99 x 76.78 x 30 mm, 6 faces (baked)
FEATURE [Part::Feature] Cut004022002_solid001  label="Cut004022002 (Solid)001"
  shape: bbox 99.53 x 106 x 44.5 mm, 121 faces (baked)
FEATURE [Part::Feature] Body001003
  shape: bbox 52.32 x 70.62 x 40 mm, 6 faces (baked)
FEATURE [Part::Cut] Cut004022026
  Base = -> Cut004022002_solid001
  Tool = -> Body001002
FEATURE [Part::Cut] Cut004022027
  Base = -> Cut004022026
  Tool = -> Body001003
FEATURE [Part::Box] Box060  label="Cube056"
  AttacherType = Attacher::AttachEngine3D
  Height = 30
  Length = 23
  Placement = pos=(-40.5,-58.5,0) rot=(0,0,1;0rad)
  Width = 58.5
FEATURE [Part::Box] Box061  label="base_sofporte_celular003"
  AttacherType = Attacher::AttachEngine3D
  Height = 40
  Length = 157.2
  Placement = pos=(-78.6,-87.5,24) rot=(0,0,1;0rad)
  Width = 25
FEATURE [Part::Box] Box062  label="Cube057"
  AttacherType = Attacher::AttachEngine3D
  Height = 30
  Length = 15
  Placement = pos=(-7.5,-58.5,0) rot=(0,0,1;0rad)
  Width = 50
FEATURE [Part::Cylinder] Cylinder004
  Angle = 360
  AttacherType = Attacher::AttachEngine3D
  FirstAngle = 0
  Height = 100
  Placement = pos=(-50,-11,13) rot=(0,1,0;1.5708rad)
  Radius = 5
  SecondAngle = 0
FEATURE [Part::Box] Box063  label="Cube058"
  AttacherType = Attacher::AttachEngine3D
  Height = 6
  Length = 93
  Placement = pos=(-46.5,-64.5,19) rot=(0,0,1;0rad)
  Width = 32
FEATURE [Part::MultiFuse] Fusion004009013
  Shapes = -> [Cut004022027,Box063]
FEATURE [Part::Cut] Cut004022025
  Base = -> Fusion004009013
  Tool = -> Box062
FEATURE [Part::Cut] Cut004022028
  Base = -> Cut004022025
  Tool = -> Box060
FEATURE [Part::Box] Box064  label="base_sofporte_celular004"
  AttacherType = Attacher::AttachEngine3D
  Height = 40
  Length = 166.2
  Width = 13
FEATURE [Part::Box] Box065  label="Cube059"
  AttacherType = Attacher::AttachEngine3D
  Height = 30
  Length = 23
  Placement = pos=(17.5,-58.5,0) rot=(0,0,1;0rad)
  Width = 58.5
FEATURE [Part::Cut] Cut004022024
  Base = -> Cut004022028
  Tool = -> Box065
FEATURE [Part::Fillet] Fillet008027011008008
  Base = -> Cut004022024
  Edges = 4 edges r=5: [Edge49,Edge53,Edge65,Edge70]
FEATURE [Part::Fillet] Fillet008027011008009
  Base = -> Fillet008027011008008
  Edges = 4 edges r=1: [Edge28,Edge47,Edge61,Edge77]
FEATURE [Part::Fillet] Fillet008027011008010
  Base = -> Fillet008027011008009
  Edges = 1 edges r=1: [Edge269]
FEATURE [Part::Fillet] Fillet008027011008011
  Base = -> Fillet008027011008010
  Edges = 1 edges r=1: [Edge347]
FEATURE [Part::Fillet] Fillet008027011008012
  Base = -> Fillet008027011008011
  Edges = 2 edges r=5: [Edge236,Edge297]
FEATURE [Part::Fillet] Fillet008027011008007
  Base = -> Fillet008027011008012
  Edges = 2 edges r=3: [Edge392,Edge439]
FEATURE [Part::Box] Box066  label="base_sofporte_celular005"
  AttacherType = Attacher::AttachEngine3D
  Height = 45
  Length = 172.2
  Placement = pos=(-3,-2.5,-5) rot=(0,0,1;0rad)
  Width = 18
FEATURE [Part::Cut] Cut004022030  label="frontal_solo_soporte001"
  Base = -> Fillet008027011008007
  Tool = -> Cylinder004
FEATURE [Part::Cut] Cut004022032
  Base = -> Box066
  Placement = pos=(-83.1,-80,20) rot=(0,0,1;0rad)
  Tool = -> Box064
FEATURE [Part::Cut] Cut004022031
  Base = -> Cut004022032
  Tool = -> Box061
FEATURE [Part::Box] Box067  label="Cube060"
  AttacherType = Attacher::AttachEngine3D
  Height = 6
  Length = 93
  Placement = pos=(-46.5,-70,19) rot=(0,0,1;0rad)
  Width = 6
FEATURE [Part::Box] Box068  label="Cube061"
  AttacherType = Attacher::AttachEngine3D
  Height = 20
  Length = 140
  Placement = pos=(-70,-80,9) rot=(0,0,1;0rad)
  Width = 13
FEATURE [Part::Cut] Cut004022029
  Base = -> Cut004022031
  Tool = -> Box068
FEATURE [Part::Fillet] Fillet008027011008018
  Base = -> Cut004022029
  Edges = 4 edges r=2: [Edge56,Edge58,Edge60,Edge62]
  Placement = pos=(0,-5,1) rot=(0,0,1;0rad)
FEATURE [Part::MultiFuse] Fusion004009012
  Refine = true
  Shapes = -> [Cut004022030,Fillet008027011008018,Box067]
FEATURE [Part::Box] Box069  label="Cube062"
  AttacherType = Attacher::AttachEngine3D
  Height = 3
  Length = 12
  Placement = pos=(-19,-86,16) rot=(0,0,1;0rad)
  Width = 15
FEATURE [Part::MultiFuse] Fusion004009014
  Refine = true
  Shapes = -> [Fusion004009012,Box069]
FEATURE [Part::Box] Box070  label="Cube063"
  AttacherType = Attacher::AttachEngine3D
  Height = 6
  Length = 12
  Placement = pos=(-19,17,0) rot=(0,0,1;0rad)
  Width = 40
FEATURE [Part::MultiFuse] Fusion004009015
  Refine = true
  Shapes = -> [Fusion004009014,Box070]
FEATURE [Part::Cut] Cut004022033
  Base = -> Fusion004009015
  Refine = true
  Tool = -> Box057
FEATURE [Part::Cut] Cut004022034
  Base = -> Cut004022033
  Refine = true
  Tool = -> Box058
FEATURE [Part::Cut] Cut004022035  label="test_v33_largo"
  Base = -> Cut004022034
  Refine = true
  Tool = -> Box059
FEATURE [Mesh::Feature] Mesh  label="test_v33_largo (Meshed)"
FEATURE [Part::Box] Box071  label="Cube064"
  AttacherType = Attacher::AttachEngine3D
  Height = 31
  Length = 93
  Placement = pos=(-46.5,-72,-10) rot=(0,0,1;0rad)
  Width = 2.5
FEATURE [Part::MultiFuse] Fusion004009016  label="union_frontal1"
  Shapes = -> [Box071,Box056]
FEATURE [Part::Box] Box072  label="Cube065"
  AttacherType = Attacher::AttachEngine3D
  Height = 31
  Length = 176
  Placement = pos=(-88,-85,19) rot=(0,0,1;0rad)
  Width = 13
FEATURE [Part::Cut] Cut004022036  label="frontal_solo_celular"
  Base = -> Cut004022017
  Tool = -> Box072
FEATURE [Sketcher::SketchObject] Sketch014
  FullyConstrained = true
  MapMode = 5
  Placement = pos=(0,0,0) rot=(0.57735,0.57735,0.57735;2.0944rad)
  Support = -> [YZ_Plane003]
  sketch-geometry (3):
    g0: LineSegment StartX=-69.5 StartY=-10 StartZ=0 EndX=-69.5 EndY=19 EndZ=0
    g1: LineSegment StartX=-69.5 StartY=19 StartZ=0 EndX=-58.9449 EndY=19 EndZ=0
    g2: LineSegment StartX=-58.9449 StartY=19 StartZ=0 EndX=-69.5 EndY=-10 EndZ=0
  constraints (9):
    c: Vertical(g0)
    c: Coincident(g0,g1)
    c: Horizontal(g1)
    c: Coincident(g1,g2)
    c: Coincident(g2,g0)
    c: Angle(g2,g0) = 0.349066
    c: DistanceY(g0,g-1) = 10
    c: DistanceY(g-1,g1) = 19
    c: DistanceX(g0,g-1) = 69.5
FEATURE [PartDesign::SubShapeBinder] Binder
  BindCopyOnChange = 0
  BindMode = 0
  ClaimChildren = false
  Context = -> Body001004 [Binder.]
  Fuse = false
  MakeFace = true
  OffsetFill = false
  OffsetIntersection = false
  OffsetJoinType = 0
  OffsetOpenResult = false
  PartialLoad = false
  Refine = true
  Relative = true
  Support = -> [Sketch014]
  _Version = 2
FEATURE [PartDesign::Pad] Pad002
  Direction = (1,1,1)
  Length = 93
  Length2 = 100
  Midplane = true
  Profile = -> Binder
  Type = 0
FEATURE [PartDesign::Body] Body001004
  Group = -> [Binder,Pad002]
  Origin = -> Origin002
  Tip = -> Pad002
FEATURE [Part::MultiFuse] Fusion004009017  label="union_frontal002"
  Placement = pos=(0,0,10) rot=(0,0,1;0rad)
  Shapes = -> [Fusion004009016,Body001004]
FEATURE [Part::Fillet] Fillet008027011008019
  Base = -> Cut004022036
  Edges = 2 edges r=10: [Edge7,Edge29]
FEATURE [Part::Fillet] Fillet008027011008020
  Base = -> Fillet008027011008019
  Edges = 2 edges r=3: [Edge78,Edge104]
FEATURE [Part::Fillet] Fillet008027011008021
  Base = -> Fillet008027011008020
  Edges = 15 edges r=1: [Edge32,Edge53,Edge64,Edge72,Edge80,Edge89,Edge93,Edge95,Edge97,Edge99,Edge100,Edge101,Edge104,Edge106,Edge107]
FEATURE [Part::Fillet] Fillet008027011008022
  Base = -> Fillet008027011008021
  Edges = 3 edges r=1: [Edge79,Edge86,Edge90]
FEATURE [Part::Fillet] Fillet008027011008023  label="soporte_celular_frontal1"
  Base = -> Fillet008027011008022
  Edges = 10 edges r=1: [Edge17,Edge23,Edge27,Edge54,Edge58,Edge60,Edge89,Edge92,Edge95,Edge103]
  Placement = pos=(0,0,10) rot=(0,0,1;0rad)
FEATURE [Part::Box] Box073  label="Cube066"
  AttacherType = Attacher::AttachEngine3D
  Height = 12
  Length = 93
  Placement = pos=(-46.5,-72,25) rot=(0,0,1;0rad)
  Width = 14
FEATURE [Part::Cut] Cut004022037  label="union_frontal"
  Base = -> Fusion004009017
  Tool = -> Box073
FEATURE [Part::Fillet] Fillet008027011008024  label="union_frontal_redondeado"
  Base = -> Cut004022037
  Edges = 1 edges r=5: [Edge10]
FEATURE [Part::Fillet] Fillet008027011008025  label="frontal_celular_redondeado"
  Base = -> Fillet008027011008023
  Edges = 2 edges r=1: [Edge69,Edge121]
FEATURE [Part::MultiFuse] Fusion004009018
  Shapes = -> [Fillet008027011008025,Fillet008027011008024,Cut004022008]
FEATURE [Part::Fillet] Fillet008027011008026  label="soporte_v4"
  Base = -> Fusion004009018
  Edges = 2 edges r=5: [Edge156,Edge212]
FEATURE [Mesh::Feature] Mesh003  label="soporte_v4 (Meshed)"
FEATURE [Part::Feature] Fillet008027011008026001  label="soporte_v4_tablet1"
  shape: bbox 172.2 x 148.5 x 45 mm, 254 faces (baked)
FEATURE [Part::Feature] Fillet008027011008026002  label="soporte_v4_tablet2"
  shape: bbox 172.2 x 148.5 x 45 mm, 254 faces (baked)
FEATURE [Part::Feature] Fillet008027011008026003  label="soporte_v4_tablet3"
  shape: bbox 172.2 x 148.5 x 45 mm, 254 faces (baked)
FEATURE [Part::Box] Box074  label="Cube067"
  AttacherType = Attacher::AttachEngine3D
  Height = 80
  Length = 200
  Placement = pos=(-54,-111,-5) rot=(0,0,1;0rad)
  Width = 200
FEATURE [Part::Box] Box075  label="Cube068"
  AttacherType = Attacher::AttachEngine3D
  Height = 80
  Length = 200
  Placement = pos=(-254,-111,-5) rot=(0,0,1;0rad)
  Width = 200
FEATURE [Part::Box] Box076  label="Cube069"
  AttacherType = Attacher::AttachEngine3D
  Height = 80
  Length = 200
  Placement = pos=(-146,-111,-5) rot=(0,0,1;0rad)
  Width = 200
FEATURE [Part::Box] Box078  label="Cube071"
  AttacherType = Attacher::AttachEngine3D
  Height = 80
  Length = 200
  Placement = pos=(54,-111,-5) rot=(0,0,1;0rad)
  Width = 200
FEATURE [Part::Cut] Cut004022038  label="izquierda"
  Base = -> Fillet008027011008026001
  Placement = pos=(-6.9,0,0) rot=(0,0,1;0rad)
  Tool = -> Box074
FEATURE [Part::Cut] Cut004022039
  Base = -> Fillet008027011008026002
  Tool = -> Box078
FEATURE [Part::Cut] Cut004022040  label="centro"
  Base = -> Cut004022039
  Tool = -> Box075
FEATURE [Part::Cut] Cut004022041  label="derecha"
  Base = -> Fillet008027011008026003
  Placement = pos=(6.9,0,0) rot=(0,0,1;0rad)
  Tool = -> Box076
FEATURE [Part::Box] Box079  label="Cube072"
  AttacherType = Attacher::AttachEngine3D
  Height = 9
  Length = 10.9
  Placement = pos=(-64,-87.5,0) rot=(0,0,1;0rad)
  Width = 2.5
FEATURE [Part::Box] Box080  label="Cube073"
  AttacherType = Attacher::AttachEngine3D
  Height = 9
  Length = 10.9
  Placement = pos=(-64,-72,0) rot=(0,0,1;0rad)
  Width = 2.5
FEATURE [Part::Box] Box081  label="Cube074"
  AttacherType = Attacher::AttachEngine3D
  Height = 9
  Length = 10.9
  Placement = pos=(53,-87.5,0) rot=(0,0,1;0rad)
  Width = 2.5
FEATURE [Part::Box] Box082  label="Cube075"
  AttacherType = Attacher::AttachEngine3D
  Height = 9
  Length = 10.9
  Placement = pos=(52,-72,0) rot=(0,0,1;0rad)
  Width = 2.5
FEATURE [Part::MultiFuse] Fusion004009019
  Shapes = -> [Cut004022038,Cut004022040,Cut004022041,Box079,Box080,Box081,Box082]
FEATURE [Part::Box] Box083  label="Cube076"
  AttacherType = Attacher::AttachEngine3D
  Height = 5
  Length = 14
  Placement = pos=(-7,-87,0) rot=(0,0,1;0rad)
  Width = 18
FEATURE [Part::MultiFuse] Fusion004009020  label="soporte_v4_tablet_lenovo"
  Shapes = -> [Fusion004009019,Box083]
FEATURE [Mesh::Feature] Mesh004  label="soporte_v4_tablet_lenovo (Meshed)"
FEATURE [Part::Box] Box084  label="Cube077"
  AttacherType = Attacher::AttachEngine3D
  Height = 72.5
  Length = 112.5
  Placement = pos=(-26.5,-67,19) rot=(0,0,1;0rad)
  Width = 15
FEATURE [Part::Feature] Fillet008027011008_solid002  label="soporte_v3_2 (Solid)002"
  shape: bbox 173.7 x 143.7 x 61.22 mm, 236 faces (baked)
FEATURE [Part::Cut] Cut004022042
  Base = -> Box084
  Tool = -> Fillet008027011008_solid002
FEATURE [Part::Box] Box085  label="Cube078"
  AttacherType = Attacher::AttachEngine3D
  Height = 70
  Length = 112.5
  Placement = pos=(-26.5,-56.5,91.5) rot=(0,0,1;0rad)
  Width = 4.5
FEATURE [Part::Box] Box086  label="Cube079"
  AttacherType = Attacher::AttachEngine3D
  Height = 136.5
  Length = 10
  Placement = pos=(-36.5,-67,25) rot=(0,0,1;0rad)
  Width = 15
FEATURE [Part::MultiFuse] Fusion004009021
  Shapes = -> [Cut004022042,Box085,Box086]
FEATURE [Part::Fillet] Fillet008027011008026004
  Base = -> Fusion004009021
  Edges = 1 edges r=5: [Edge2]
FEATURE [Part::Fillet] Fillet008027011008026005
  Base = -> Fillet008027011008026004
  Edges = 1 edges r=5: [Edge70]
FEATURE [Part::Fillet] Fillet008027011008026006
  Base = -> Fillet008027011008026005
  Edges = 1 edges r=2: [Edge38]
FEATURE [Part::Fillet] Fillet008027011008026007  label="soporte_over_soporteV1"
  Base = -> Fillet008027011008026006
  Edges = 4 edges r=1: [Edge11,Edge22,Edge39,Edge50]
FEATURE [Part::Feature] Fillet008027011008026007001  label="soporte_over_soporteV2111"
  shape: bbox 123.3 x 15.16 x 142.9 mm, 60 faces (baked)
FEATURE [Part::Box] Box087  label="Cube080"
  AttacherType = Attacher::AttachEngine3D
  Height = 95.5
  Length = 22.9
  Width = 40
FEATURE [Part::Fillet] Fillet008027011008026007002
  Base = -> Box087
  Edges = 4 edges r=10: [Edge2,Edge4,Edge6,Edge8]
  Placement = pos=(52.05,-74,46) rot=(0,0,1;0rad)
FEATURE [Part::Feature] Fillet008027011008026007002001
  Placement = pos=(-16.2,-74,46) rot=(0,0,1;0rad)
  shape: bbox 22.9 x 40 x 95.5 mm, 10 faces (baked)
FEATURE [Part::Feature] Fillet008027011008026007002002
  Placement = pos=(18.15,-74,46) rot=(0,0,1;0rad)
  shape: bbox 22.9 x 40 x 95.5 mm, 10 faces (baked)
FEATURE [Part::Cut] Cut004022043
  Base = -> Fillet008027011008026007001
  Tool = -> Fillet008027011008026007002
FEATURE [Part::Cut] Cut004022044
  Base = -> Cut004022043
  Tool = -> Fillet008027011008026007002001
FEATURE [Part::Cut] Cut004022045
  Base = -> Cut004022044
  Tool = -> Fillet008027011008026007002002
FEATURE [Part::Box] Box088  label="Cube081"
  AttacherType = Attacher::AttachEngine3D
  Height = 10
  Length = 97
  Placement = pos=(-18,-67,81.5) rot=(0,0,1;0rad)
  Width = 15
FEATURE [Part::MultiFuse] Fusion004009022
  Shapes = -> [Cut004022045,Box088]
FEATURE [Part::Fillet] Fillet008027011008026007002003
  Base = -> Fusion004009022
  Edges = 6 edges r=10: [Edge156,Edge165,Edge169,Edge178,Edge181,Edge190]
FEATURE [Part::Box] Box089  label="Cube082"
  AttacherType = Attacher::AttachEngine3D
  Height = 10
  Length = 10
  Placement = pos=(80,-74.5,18) rot=(0,0,1;0rad)
  Width = 10
FEATURE [Part::Cut] Cut004022046  label="soporte_over_soporteV3_1"
  Base = -> Fillet008027011008026007002003
  Tool = -> Box089
FEATURE [Part::Box] Box090  label="Cube083"
  AttacherType = Attacher::AttachEngine3D
  Height = 20
  Length = 22.5
  Placement = pos=(-36.5,-70.5,141.5) rot=(0,0,1;0rad)
  Width = 8.5
FEATURE [Part::MultiFuse] Fusion004009023
  Shapes = -> [Cut004022046,Box090]
FEATURE [Part::Fillet] Fillet008027011008026007002004
  Base = -> Fusion004009023
  Edges = 2 edges r=3.5: [Edge25,Edge27]
FEATURE [Part::Fillet] Fillet008027011008026007002005
  Base = -> Fillet008027011008026007002004
  Edges = 1 edges r=4.9: [Edge7]
FEATURE [Part::Fillet] Fillet008027011008026007002006
  Base = -> Fillet008027011008026007002005
  Edges = 5 edges r=2: [Edge20,Edge21,Edge23,Edge25,Edge27]
FEATURE [Part::Fillet] Fillet008027011008026007002007  label="soporte_over_soporteV3"
  Base = -> Fillet008027011008026007002006
  Edges = 1 edges r=1: [Edge29]
FEATURE [Mesh::Feature] Mesh005  label="soporte_over_soporteV3 (Meshed)"
